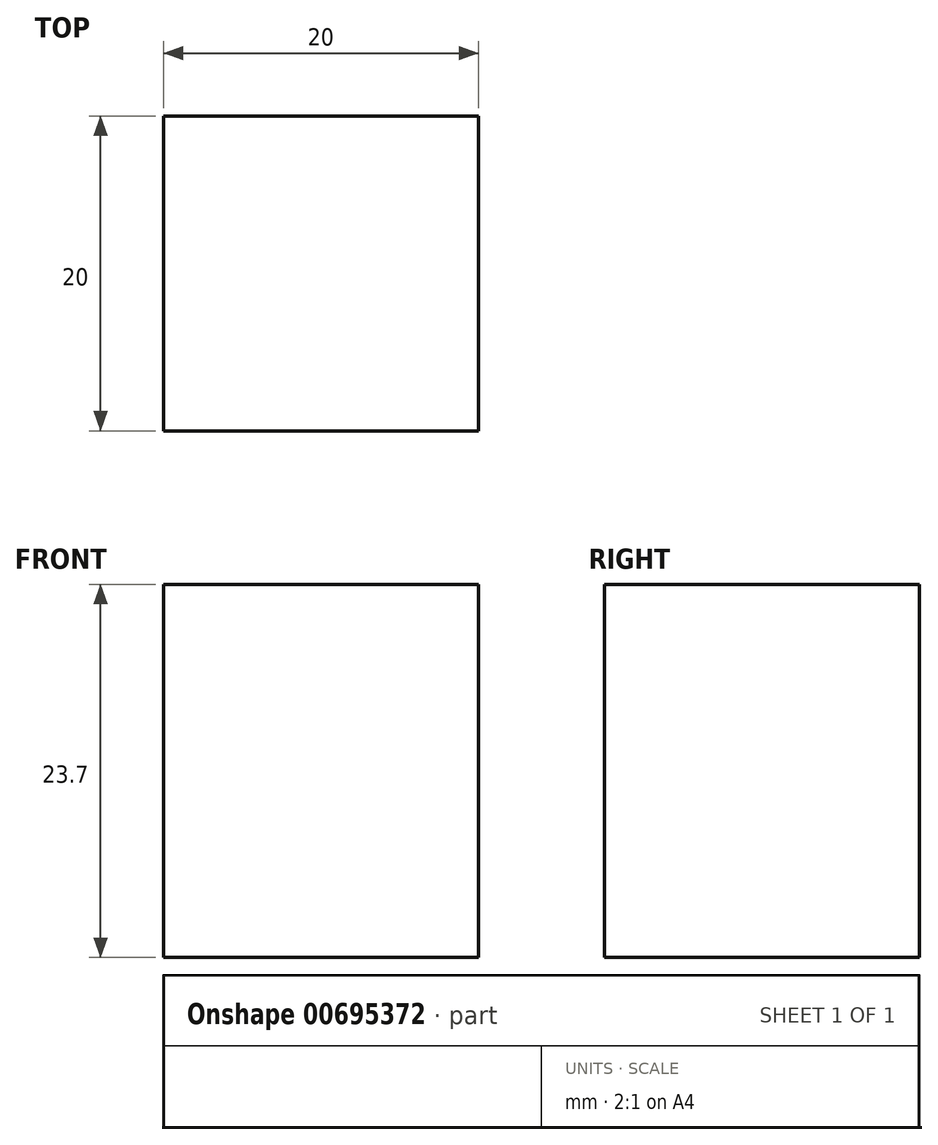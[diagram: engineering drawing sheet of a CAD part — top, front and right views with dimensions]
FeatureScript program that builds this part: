
annotation { "Feature Type Name" : "Feature", "Feature Type Description" : "" }
export const myFeature = defineFeature(function(context is Context, id is Id, definition is map)
    precondition{}
    {
        {
            var Q0;
            Q0=qCreatedBy(makeId("Top.planeOp"),FACE);
            var sketch = newSketch(context, id + "F0", { "sketchPlane" : qUnion([Q0])});
            skLineSegment(sketch, "E0.bottom", {"start": v(10, 10) * mm, "end": v(-10, 10) * mm});
            skLineSegment(sketch, "E0.top", {"start": v(10, -10) * mm, "end": v(-10, -10) * mm});
            skLineSegment(sketch, "E0.left", {"start": v(10, 10) * mm, "end": v(10, -10) * mm});
            skLineSegment(sketch, "E0.right", {"start": v(-10, 10) * mm, "end": v(-10, -10) * mm});
            skPoint(sketch, "E0.middle", {"position": v(0, 0) * mm});
            skSolve(sketch);
        }
        {
            var Q0;
            Q0 = qSketchRegion(id + "F0", true);
            extrude(context, id + "F1", {"entities" : qUnion([Q0]), "depth" : 23.7 * mm, "offsetDistance" : 25.4 * mm});
        }
    });
